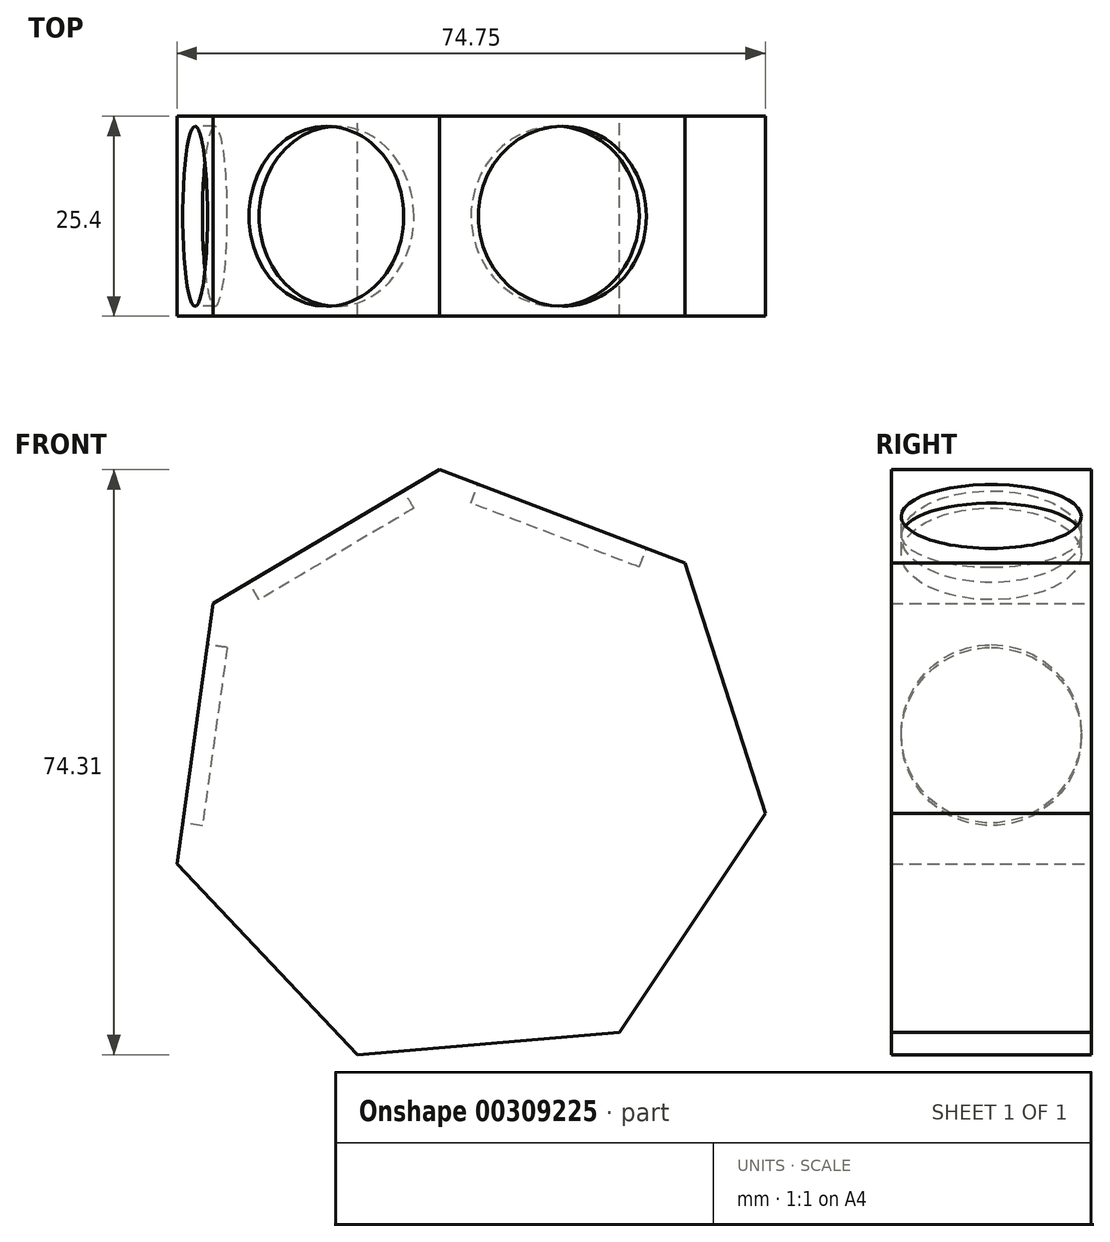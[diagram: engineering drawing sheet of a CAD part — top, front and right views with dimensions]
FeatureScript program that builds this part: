
annotation { "Feature Type Name" : "Feature", "Feature Type Description" : "" }
export const myFeature = defineFeature(function(context is Context, id is Id, definition is map)
    precondition{}
    {
        {
            var Q0;
            Q0=qCreatedBy(makeId("Front.planeOp"),FACE);
            var sketch = newSketch(context, id + "F0", { "sketchPlane" : qUnion([Q0])});
            skCircle(sketch, "E0.cCircle", {"center": v(0, 0) * mm, "radius": 38.48 * mm, "construction": true});
            skLineSegment(sketch, "E0.0", {"start": v(27.92, 26.48) * mm, "end": v(38.1, -5.32) * mm});
            skLineSegment(sketch, "E0.1", {"start": v(38.1, -5.32) * mm, "end": v(19.6, -33.1) * mm});
            skLineSegment(sketch, "E0.2", {"start": v(19.6, -33.1) * mm, "end": v(-13.66, -35.97) * mm});
            skLineSegment(sketch, "E0.3", {"start": v(-13.66, -35.97) * mm, "end": v(-36.64, -11.74) * mm});
            skLineSegment(sketch, "E0.4", {"start": v(-36.64, -11.74) * mm, "end": v(-32.03, 21.33) * mm});
            skLineSegment(sketch, "E0.5", {"start": v(-32.03, 21.33) * mm, "end": v(-3.3, 38.34) * mm});
            skLineSegment(sketch, "E0.6", {"start": v(-3.3, 38.34) * mm, "end": v(27.92, 26.48) * mm});
            skSolve(sketch);
        }
        {
            var Q0;
            Q0 = qSketchRegion(id + "F0", true);
            extrude(context, id + "F1", {"entities" : qUnion([Q0]), "depth" : 25.4 * mm});
        }
        {
            var Q0;
            Q0=makeQuery(id+"F1.opExtrude","SWEPT_FACE",FACE,{"disambiguationData":[OSD([sQuery(id+"F0.wireOp",EDGE,"E0.4")])]});
            var sketch = newSketch(context, id + "F2", { "sketchPlane" : qUnion([Q0])});
            skCircle(sketch, "E1", {"center": v(12.7, 0) * mm, "radius": 11.43 * mm});
            skPoint(sketch, "E1.centerSnap0", {"position": v(12.7, 16.7) * mm});
            skSolve(sketch);
        }
        {
            var Q0;
            Q0=makeQuery(id+"F1.opExtrude","SWEPT_FACE",FACE,{"disambiguationData":[OSD([sQuery(id+"F0.wireOp",EDGE,"E0.5")])]});
            var sketch = newSketch(context, id + "F3", { "sketchPlane" : qUnion([Q0])});
            skCircle(sketch, "E2", {"center": v(0, -12.7) * mm, "radius": 11.43 * mm});
            skPoint(sketch, "E2.centerSnap0", {"position": v(16.7, -12.7) * mm});
            skSolve(sketch);
        }
        {
            var Q0;
            Q0=makeQuery(id+"F1.opExtrude","SWEPT_FACE",FACE,{"disambiguationData":[OSD([sQuery(id+"F0.wireOp",EDGE,"E0.6")])]});
            var sketch = newSketch(context, id + "F4", { "sketchPlane" : qUnion([Q0])});
            skCircle(sketch, "E3", {"center": v(0, -12.7) * mm, "radius": 11.43 * mm});
            skPoint(sketch, "E3.centerSnap0", {"position": v(16.7, -12.7) * mm});
            skSolve(sketch);
        }
        {
            var Q0;
            Q0 = qSketchRegion(id + "F2", true);
            extrude(context, id + "F5", {"entities" : qUnion([Q0]), "operationType" : NewBodyOperationType.REMOVE, "oppositeDirection" : true, "depth" : 2.54 * mm});
        }
        {
            var Q0;
            Q0=makeQuery(id+"F3.imprint","IMPRINT",FACE,{"disambiguationData":[TD([[makeQuery(id+"F3.imprint","IMPRINT",EDGE,{"derivedFrom":sQuery(id+"F3.wireOp",EDGE,"E2")}),1.0]])]});
            extrude(context, id + "F6", {"entities" : qUnion([Q0]), "operationType" : NewBodyOperationType.REMOVE, "oppositeDirection" : true, "depth" : 2.54 * mm});
        }
        {
            var Q0;
            Q0=makeQuery(id+"F4.imprint","IMPRINT",FACE,{"disambiguationData":[TD([[makeQuery(id+"F4.imprint","IMPRINT",EDGE,{"derivedFrom":sQuery(id+"F4.wireOp",EDGE,"E3")}),1.0]])]});
            extrude(context, id + "F7", {"entities" : qUnion([Q0]), "operationType" : NewBodyOperationType.REMOVE, "oppositeDirection" : true, "depth" : 2.54 * mm});
        }
    });
